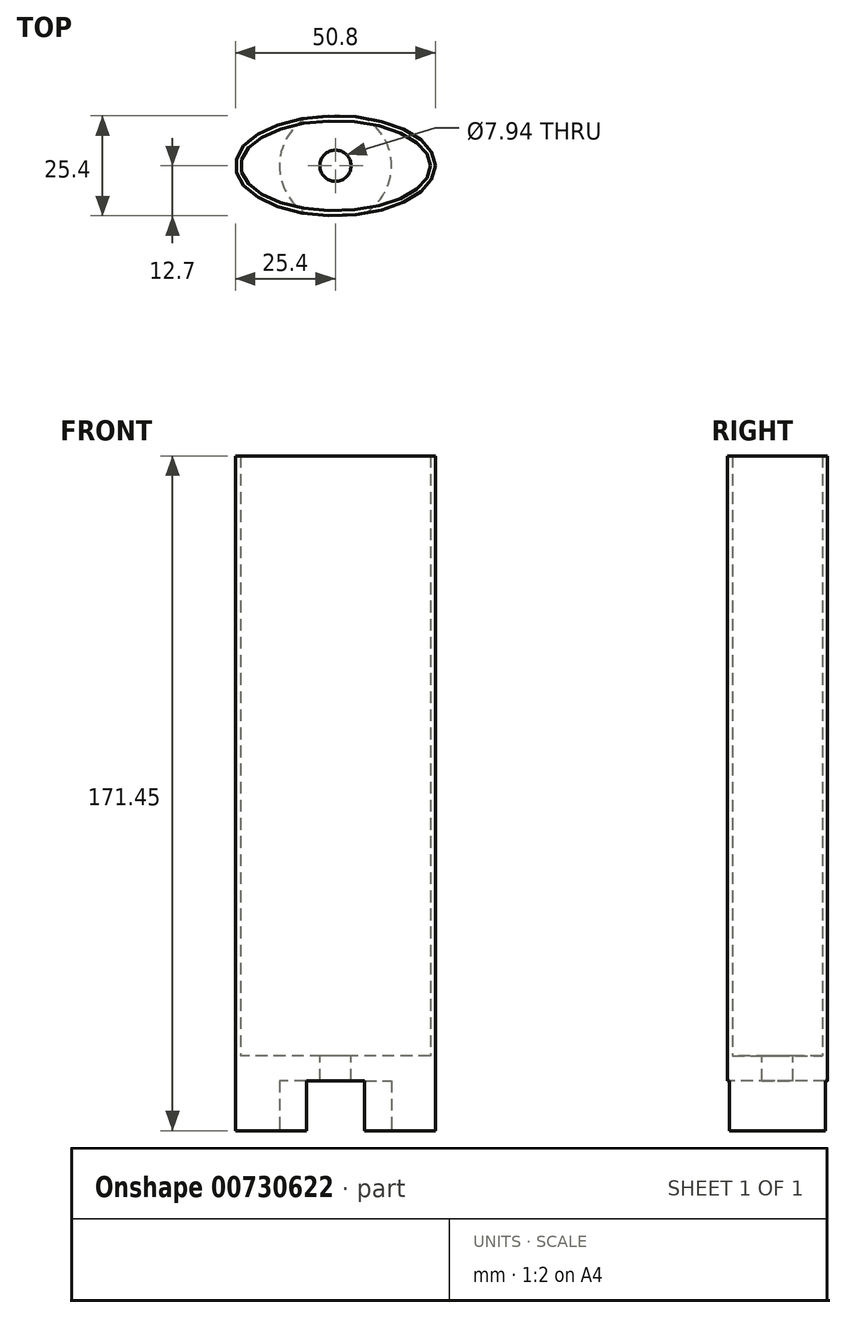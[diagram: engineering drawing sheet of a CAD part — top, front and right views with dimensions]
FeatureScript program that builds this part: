
annotation { "Feature Type Name" : "Feature", "Feature Type Description" : "" }
export const myFeature = defineFeature(function(context is Context, id is Id, definition is map)
    precondition{}
    {
        {
            var Q0;
            Q0=qCreatedBy(makeId("Top.planeOp"),FACE);
            var sketch = newSketch(context, id + "F0", { "sketchPlane" : qUnion([Q0])});
            skEllipse(sketch, "E0", {"center": v(0, 0) * mm, "majorRadius": 25.4 * mm, "minorRadius": 12.7 * mm, "majorAxis": v(1, 0)});
            skSolve(sketch);
        }
        {
            var Q0;
            Q0=makeQuery(id+"F0.imprint","IMPRINT",FACE,{"disambiguationData":[TD([[makeQuery(id+"F0.imprint","IMPRINT",EDGE,{"derivedFrom":sQuery(id+"F0.wireOp",EDGE,"E0")}),1.0]])]});
            extrude(context, id + "F1", {"entities" : qUnion([Q0]), "depth" : 19.05 * mm, "offsetDistance" : 25.4 * mm});
        }
        {
            var Q0;
            Q0=makeQuery(id+"F1.opExtrude","CAP_FACE",FACE,{"disambiguationData":[OSD([sQuery(id+"F0.wireOp",EDGE,"E0")])],"isStart":true});
            var sketch = newSketch(context, id + "F2", { "sketchPlane" : qUnion([Q0])});
            skCircle(sketch, "E1", {"center": v(0, 0) * mm, "radius": 14.22 * mm});
            skSolve(sketch);
        }
        {
            var Q0;
            {var subQ0=sQuery(id+"F2.wireOp",EDGE,"E1");var subQ1=makeQuery(id+"F1.opExtrude","CAP_EDGE",EDGE,{"disambiguationData":[OSD([sQuery(id+"F0.wireOp",EDGE,"E0")])],"isStart":true});var subQ2=makeQuery(id+"F2.imprint","INTERSECT",VERTEX,{"disambiguationData":[OD(0.0)],"derivedFrom":[subQ1,subQ0]});Q0=makeQuery(id+"F2.imprint","IMPRINT",FACE,{"disambiguationData":[TD([[makeQuery(id+"F2.imprint","IMPRINT",EDGE,{"disambiguationData":[TD([[subQ2,-1.0]])],"derivedFrom":subQ0}),1.0]])]});}
            var Q1;
            Q1=sQuery(id+"F2.wireOp",EDGE,"E1");
            extrude(context, id + "F3", {"entities" : qUnion([Q0]), "operationType" : NewBodyOperationType.REMOVE, "surfaceEntities" : qUnion([Q1]), "oppositeDirection" : true, "depth" : 12.7 * mm, "offsetDistance" : 25.4 * mm});
        }
        {
            var Q0;
            Q0=makeQuery(id+"F1.opExtrude","CAP_FACE",FACE,{"disambiguationData":[OSD([sQuery(id+"F0.wireOp",EDGE,"E0")])],"isStart":false});
            var sketch = newSketch(context, id + "F4", { "sketchPlane" : qUnion([Q0])});
            skCircle(sketch, "E2", {"center": v(0, 0) * mm, "radius": 3.97 * mm});
            skSolve(sketch);
        }
        {
            var Q0;
            Q0=makeQuery(id+"F4.imprint","IMPRINT",FACE,{"disambiguationData":[TD([[makeQuery(id+"F4.imprint","IMPRINT",EDGE,{"derivedFrom":sQuery(id+"F4.wireOp",EDGE,"E2")}),1.0]])]});
            var Q1;
            Q1=sQuery(id+"F4.wireOp",EDGE,"E2");
            extrude(context, id + "F5", {"entities" : qUnion([Q0]), "operationType" : NewBodyOperationType.REMOVE, "surfaceEntities" : qUnion([Q1]), "oppositeDirection" : true, "depth" : 6.35 * mm, "offsetDistance" : 25.4 * mm});
        }
        {
            var Q0;
            Q0=makeQuery(id+"F1.opExtrude","CAP_FACE",FACE,{"disambiguationData":[OSD([sQuery(id+"F0.wireOp",EDGE,"E0")])],"isStart":false});
            var sketch = newSketch(context, id + "F6", { "sketchPlane" : qUnion([Q0])});
            skEllipse(sketch, "E3", {"center": v(0, 0) * mm, "majorRadius": 25.4 * mm, "minorRadius": 12.7 * mm, "majorAxis": v(1, 0)});
            skEllipse(sketch, "E4", {"center": v(0, 0) * mm, "majorRadius": 24.13 * mm, "minorRadius": 11.43 * mm, "majorAxis": v(1, 0)});
            skSolve(sketch);
        }
        {
            var Q0;
            Q0=makeQuery(id+"F6.imprint","IMPRINT",FACE,{"disambiguationData":[TD([[makeQuery(id+"F6.imprint","IMPRINT",EDGE,{"derivedFrom":sQuery(id+"F6.wireOp",EDGE,"E3")}),1.0]])]});
            var Q1;
            Q1 = qSketchRegion(id + "F6", true);
            extrude(context, id + "F7", {"entities" : qUnion([Q0, Q1]), "operationType" : NewBodyOperationType.ADD, "depth" : 152.4 * mm, "offsetDistance" : 25.4 * mm});
        }
    });
